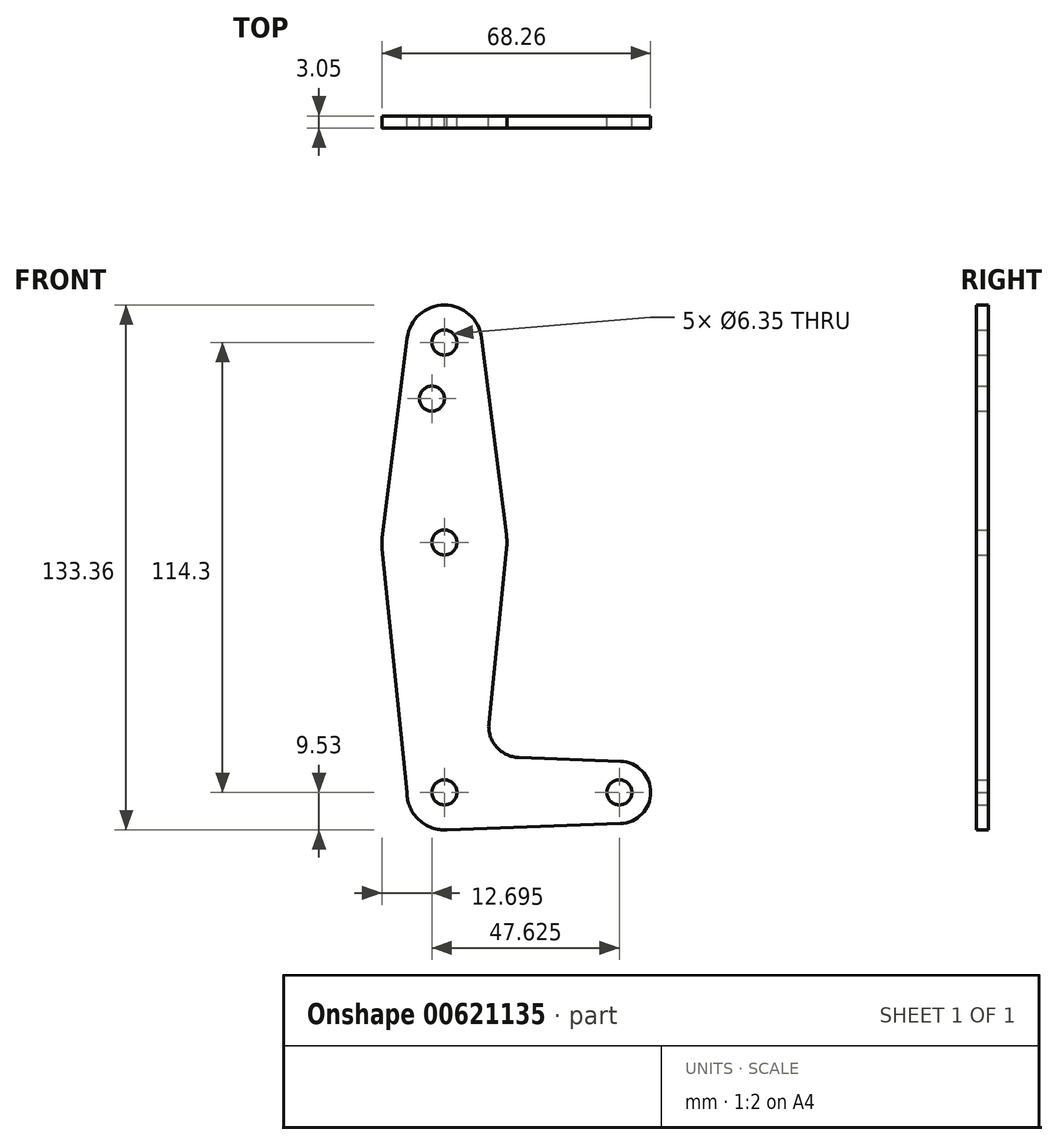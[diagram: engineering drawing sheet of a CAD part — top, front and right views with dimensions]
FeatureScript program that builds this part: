
annotation { "Feature Type Name" : "Feature", "Feature Type Description" : "" }
export const myFeature = defineFeature(function(context is Context, id is Id, definition is map)
    precondition{}
    {
        {
            var Q0;
            Q0=qCreatedBy(makeId("Front.planeOp"),FACE);
            var sketch = newSketch(context, id + "F0", { "sketchPlane" : qUnion([Q0])});
            skLineSegment(sketch, "E0", {"start": v(0, 0) * mm, "end": v(0, 114.3) * mm, "construction": true});
            skLineSegment(sketch, "E1", {"start": v(0, 0) * mm, "end": v(44.45, 0) * mm, "construction": true});
            skCircle(sketch, "E2", {"center": v(0, 0) * mm, "radius": 9.53 * mm});
            skCircle(sketch, "E3", {"center": v(44.45, 0) * mm, "radius": 7.94 * mm});
            skCircle(sketch, "E4", {"center": v(0, 114.3) * mm, "radius": 9.53 * mm});
            skCircle(sketch, "E5", {"center": v(0, 63.5) * mm, "radius": 15.88 * mm});
            skLineSegment(sketch, "E6", {"start": v(-9.53, 0) * mm, "end": v(-15.8, 61.9) * mm});
            skLineSegment(sketch, "E7", {"start": v(0, -9.53) * mm, "end": v(44.73, -7.93) * mm});
            skLineSegment(sketch, "E8", {"start": v(-9.45, 115.5) * mm, "end": v(-15.75, 65.48) * mm});
            skLineSegment(sketch, "E9.MirrorCS", {"start": v(11.3, 17.6) * mm, "end": v(15.8, 61.9) * mm});
            skLineSegment(sketch, "E10.MirrorCS", {"start": v(18.93, 8.85) * mm, "end": v(44.73, 7.93) * mm});
            skLineSegment(sketch, "E11.MirrorCS", {"start": v(9.45, 115.5) * mm, "end": v(15.75, 65.48) * mm});
            skCircle(sketch, "E12", {"center": v(0, 114.3) * mm, "radius": 3.18 * mm});
            skCircle(sketch, "E13", {"center": v(0, 63.5) * mm, "radius": 3.18 * mm});
            skCircle(sketch, "E14", {"center": v(0, 0) * mm, "radius": 3.18 * mm});
            skCircle(sketch, "E15", {"center": v(44.45, 0) * mm, "radius": 3.18 * mm});
            skPoint(sketch, "E16.newPointA", {"position": v(0, 9.53) * mm});
            skPoint(sketch, "E16.newPointB", {"position": v(9.53, 0) * mm});
            skArc(sketch, "E16.filletArc", {"start": v(11.3, 17.6) * mm, "mid": v(13.22, 11.57) * mm, "end": v(18.93, 8.85) * mm});
            skCircle(sketch, "E17", {"center": v(-3.18, 100.03) * mm, "radius": 3.18 * mm});
            skSolve(sketch);
        }
        {
            var Q0;
            Q0 = qSketchRegion(id + "F0", true);
            extrude(context, id + "F1", {"entities" : qUnion([Q0]), "depth" : 3.05 * mm, "offsetDistance" : 25.4 * mm});
        }
    });
